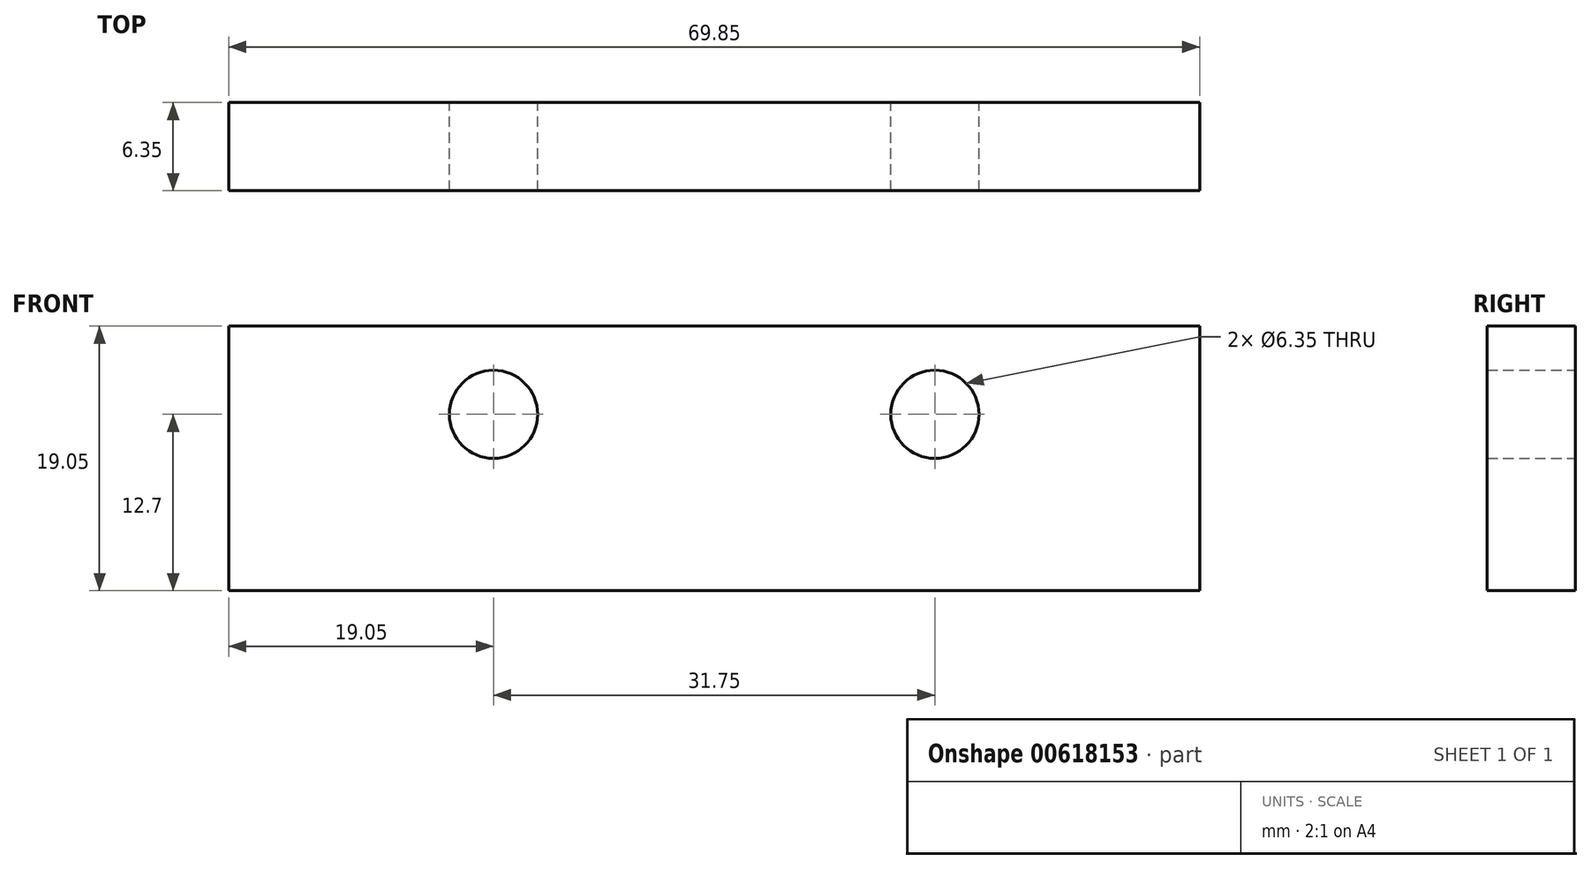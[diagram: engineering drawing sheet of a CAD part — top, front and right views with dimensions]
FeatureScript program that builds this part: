
annotation { "Feature Type Name" : "Feature", "Feature Type Description" : "" }
export const myFeature = defineFeature(function(context is Context, id is Id, definition is map)
    precondition{}
    {
        {
            var Q0;
            Q0=qCreatedBy(makeId("Front.planeOp"),FACE);
            var sketch = newSketch(context, id + "F0", { "sketchPlane" : qUnion([Q0])});
            skLineSegment(sketch, "E0.bottom", {"start": v(0, 0) * mm, "end": v(69.85, 0) * mm});
            skLineSegment(sketch, "E0.top", {"start": v(0, 19.05) * mm, "end": v(69.85, 19.05) * mm});
            skLineSegment(sketch, "E0.left", {"start": v(0, 0) * mm, "end": v(0, 19.05) * mm});
            skLineSegment(sketch, "E0.right", {"start": v(69.85, 0) * mm, "end": v(69.85, 19.05) * mm});
            skCircle(sketch, "E1", {"center": v(19.05, 12.7) * mm, "radius": 3.18 * mm});
            skCircle(sketch, "E2", {"center": v(50.8, 12.7) * mm, "radius": 3.18 * mm});
            skSolve(sketch);
        }
        {
            var Q0;
            Q0=qSketchRegion(id+"F0",true);
            extrude(context, id + "F1", {"entities" : qUnion([Q0]), "depth" : 6.35 * mm});
        }
    });
